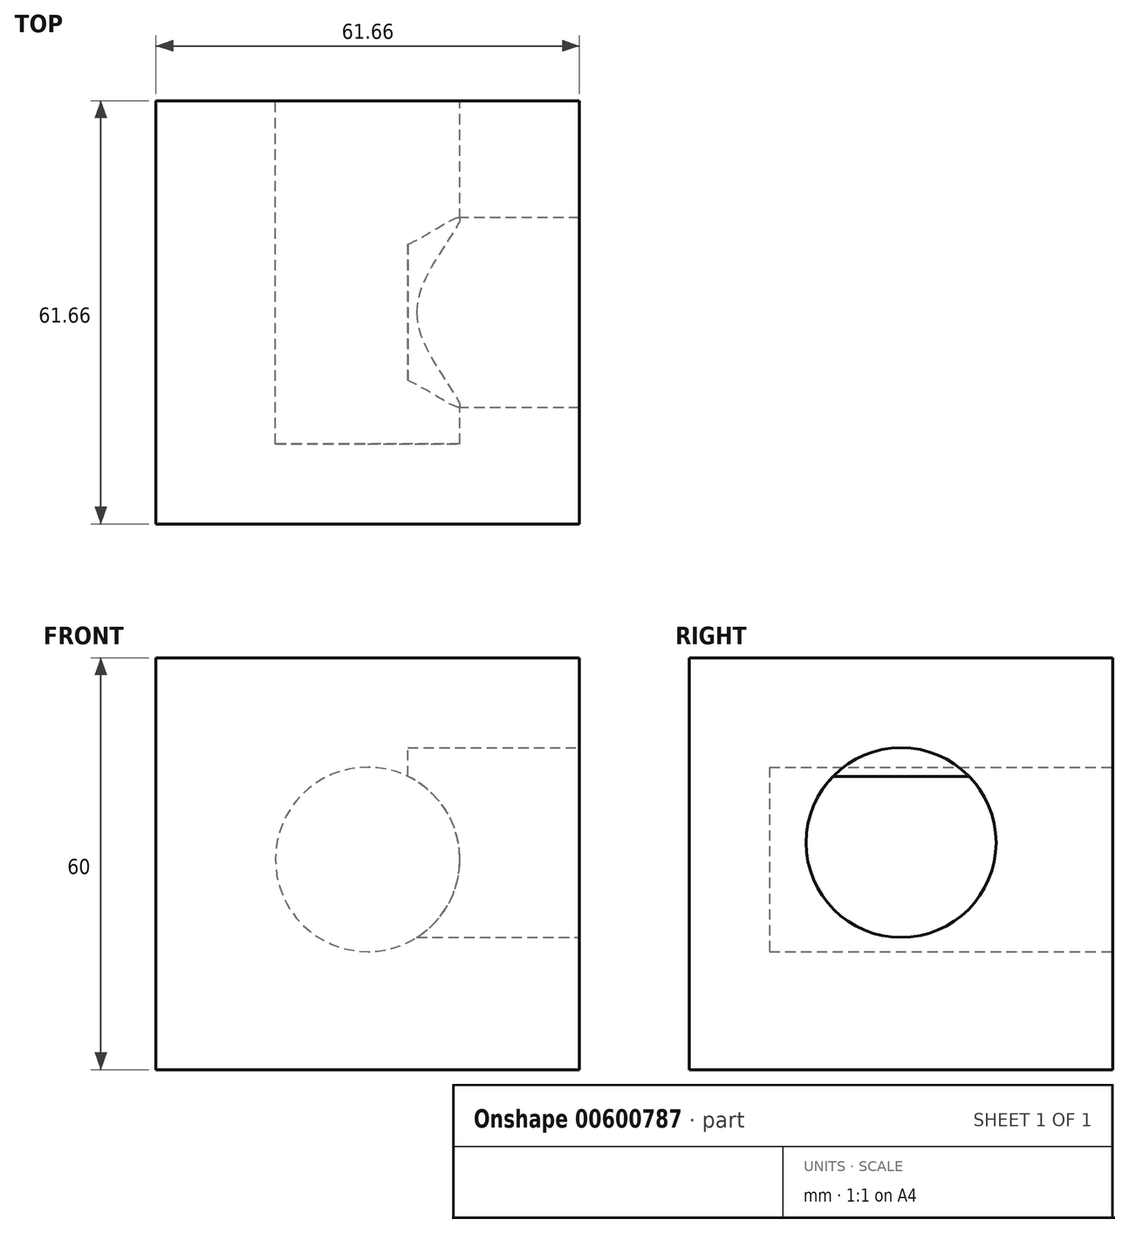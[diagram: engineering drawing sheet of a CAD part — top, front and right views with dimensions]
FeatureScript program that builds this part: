
annotation { "Feature Type Name" : "Feature", "Feature Type Description" : "" }
export const myFeature = defineFeature(function(context is Context, id is Id, definition is map)
    precondition{}
    {
        {
            var Q0;
            Q0=qCreatedBy(makeId("Top.planeOp"),FACE);
            var sketch = newSketch(context, id + "F0", { "sketchPlane" : qUnion([Q0])});
            skLineSegment(sketch, "E0.bottom", {"start": v(30.83, 30.83) * mm, "end": v(-30.83, 30.83) * mm});
            skLineSegment(sketch, "E0.top", {"start": v(30.83, -30.83) * mm, "end": v(-30.83, -30.83) * mm});
            skLineSegment(sketch, "E0.left", {"start": v(30.83, 30.83) * mm, "end": v(30.83, -30.83) * mm});
            skLineSegment(sketch, "E0.right", {"start": v(-30.83, 30.83) * mm, "end": v(-30.83, -30.83) * mm});
            skPoint(sketch, "E0.middle", {"position": v(0, 0) * mm});
            skSolve(sketch);
        }
        {
            var Q0;
            Q0=makeQuery(id+"F0.imprint","IMPRINT",FACE,{"disambiguationData":[TD([[makeQuery(id+"F0.imprint","IMPRINT",EDGE,{"derivedFrom":sQuery(id+"F0.wireOp",EDGE,"E0.bottom")}),1.0]])]});
            extrude(context, id + "F1", {"entities" : qUnion([Q0]), "depth" : 60 * mm, "offsetDistance" : 25 * mm});
        }
        {
            var Q0;
            Q0=makeQuery(id+"F1.opExtrude","SWEPT_FACE",FACE,{"disambiguationData":[OSD([sQuery(id+"F0.wireOp",EDGE,"E0.left")])]});
            var sketch = newSketch(context, id + "F2", { "sketchPlane" : qUnion([Q0])});
            skCircle(sketch, "E1", {"center": v(0, 33.08) * mm, "radius": 13.83 * mm});
            skSolve(sketch);
        }
        {
            var Q0;
            Q0 = qSketchRegion(id + "F2", true);
            extrude(context, id + "F3", {"entities" : qUnion([Q0]), "operationType" : NewBodyOperationType.REMOVE, "oppositeDirection" : true, "depth" : 25 * mm, "offsetDistance" : 25 * mm});
        }
        {
            var Q0;
            Q0=makeQuery(id+"F1.opExtrude","SWEPT_FACE",FACE,{"disambiguationData":[OSD([sQuery(id+"F0.wireOp",EDGE,"E0.bottom")])]});
            var sketch = newSketch(context, id + "F4", { "sketchPlane" : qUnion([Q0])});
            skCircle(sketch, "E2", {"center": v(0, 30.42) * mm, "radius": 16.84 * mm});
            skSolve(sketch);
        }
        {
            var Q0;
            Q0 = qSketchRegion(id + "F4", true);
            extrude(context, id + "F5", {"entities" : qUnion([Q0]), "operationType" : NewBodyOperationType.REMOVE, "depth" : 50 * mm, "offsetDistance" : 25 * mm});
        }
        {
            var Q0;
            Q0=makeQuery(id+"F1.opExtrude","SWEPT_FACE",FACE,{"disambiguationData":[OSD([sQuery(id+"F0.wireOp",EDGE,"E0.bottom")])]});
            var sketch = newSketch(context, id + "F6", { "sketchPlane" : qUnion([Q0])});
            skCircle(sketch, "E3", {"center": v(0, 30.63) * mm, "radius": 13.43 * mm});
            skSolve(sketch);
        }
        {
            var Q0;
            Q0 = qSketchRegion(id + "F6", true);
            extrude(context, id + "F7", {"entities" : qUnion([Q0]), "operationType" : NewBodyOperationType.REMOVE, "oppositeDirection" : true, "depth" : 50 * mm, "offsetDistance" : 25 * mm});
        }
    });
